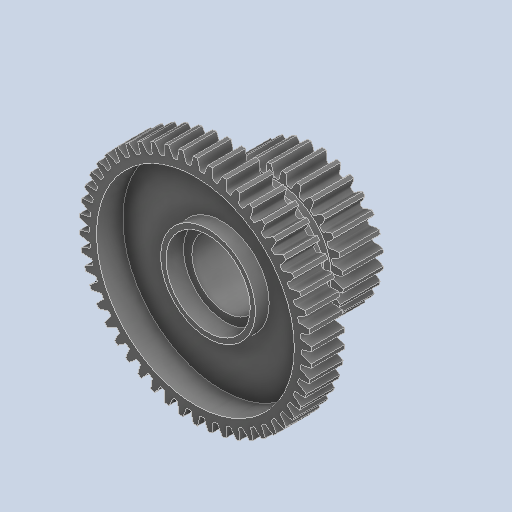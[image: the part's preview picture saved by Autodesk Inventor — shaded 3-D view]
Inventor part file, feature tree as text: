
AUTODESK INVENTOR PART (.ipt)
format: ipt  version: 2023.2 (Build 272271000, 271)  size: 733,184 bytes
history: native  units: in
note: dims shown in document units (in); Inventor stores cm internally (conversion verified against a paired STEP export)
features: chamfer x1
ambient origin geometry x8: Origin, YZ Plane, XZ Plane, XY Plane, X Axis, Y Axis, Z Axis, Center Point
bodies: Solid1 (feature_tree)
feature tree (1):
  chamfer  "Chamfer1"  [1 undecoded]
note: 1 required parameter value undecoded (feature->parameter linkage not recoverable at this tier; creation-order binding heuristic only, values carry confidence <= 0.55)
